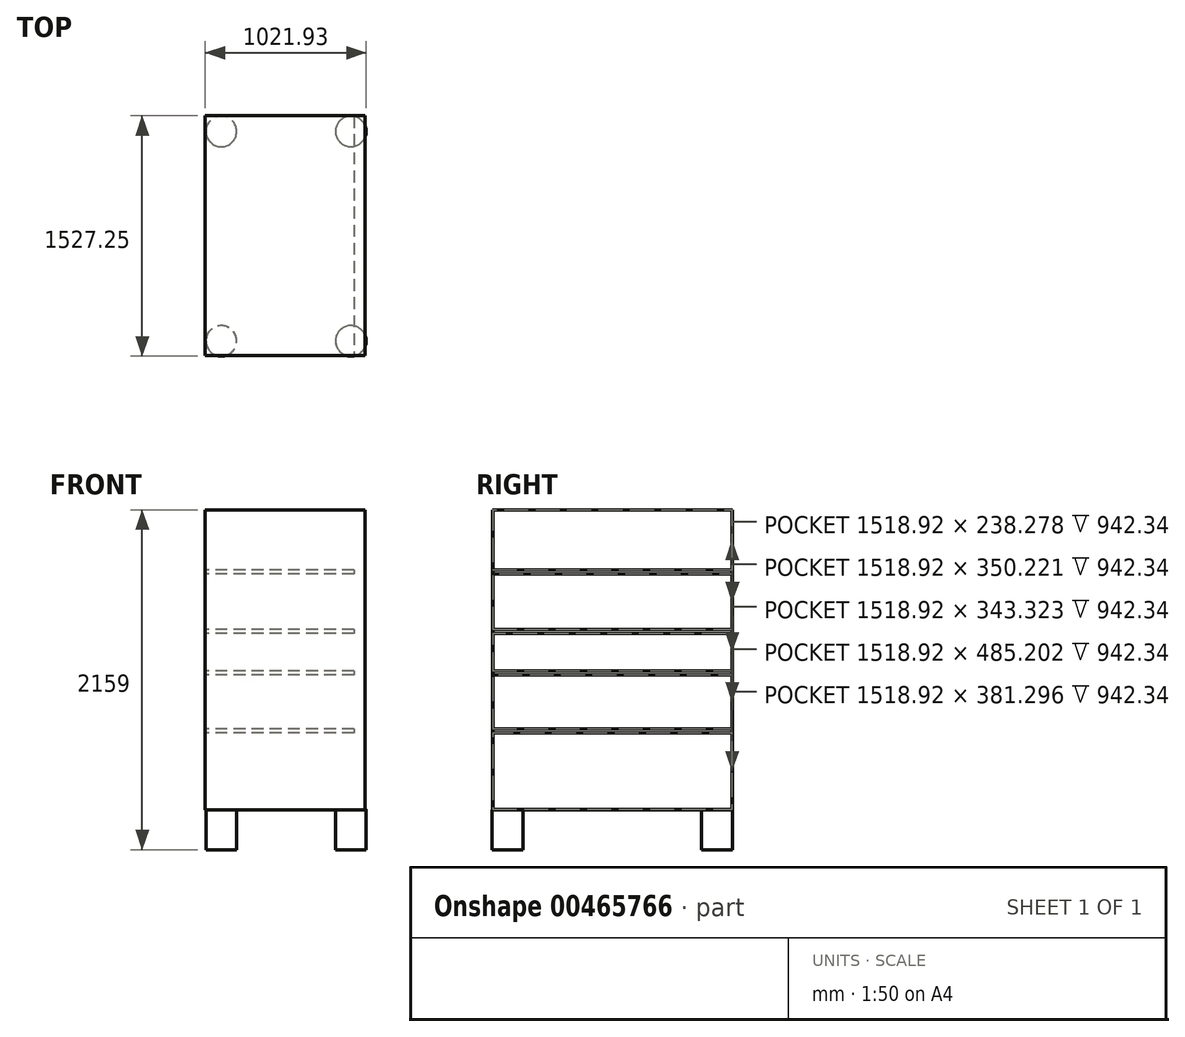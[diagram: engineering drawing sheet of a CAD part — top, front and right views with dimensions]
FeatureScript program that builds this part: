
annotation { "Feature Type Name" : "Feature", "Feature Type Description" : "" }
export const myFeature = defineFeature(function(context is Context, id is Id, definition is map)
    precondition{}
    {
        {
            var Q0;
            Q0=qCreatedBy(makeId("Right.planeOp"),FACE);
            var sketch = newSketch(context, id + "F0", { "sketchPlane" : qUnion([Q0])});
            skLineSegment(sketch, "E0.bottom", {"start": v(-808.5, 938.65) * mm, "end": v(715.5, 938.65) * mm});
            skLineSegment(sketch, "E0.top", {"start": v(-808.5, -966.35) * mm, "end": v(715.5, -966.35) * mm});
            skLineSegment(sketch, "E0.left", {"start": v(-808.5, 938.65) * mm, "end": v(-808.5, -966.35) * mm});
            skLineSegment(sketch, "E0.right", {"start": v(715.5, 938.65) * mm, "end": v(715.5, -966.35) * mm});
            skSolve(sketch);
        }
        {
            var Q0;
            Q0=makeQuery(id+"F0.imprint","IMPRINT",FACE,{"disambiguationData":[TD([[makeQuery(id+"F0.imprint","IMPRINT",EDGE,{"derivedFrom":sQuery(id+"F0.wireOp",EDGE,"E0.bottom")}),-1.0]])]});
            extrude(context, id + "F1", {"entities" : qUnion([Q0]), "depth" : 1016 * mm});
        }
        {
            var Q0;
            Q0=makeQuery(id+"F1.opExtrude","CAP_FACE",FACE,{"disambiguationData":[OSD([sQuery(id+"F0.wireOp",EDGE,"E0.bottom"),sQuery(id+"F0.wireOp",EDGE,"E0.top"),sQuery(id+"F0.wireOp",EDGE,"E0.left"),sQuery(id+"F0.wireOp",EDGE,"E0.right")])],"isStart":false});
            shell(context, id + "F2", {"entities" : qUnion([Q0]), "thickness" : 2.54 * mm});
        }
        {
            var Q0;
            Q0=makeQuery(id+"F2.opShell","OFFSET_FACE",FACE,{"disambiguationData":[OSD([sQuery(id+"F0.wireOp",EDGE,"E0.bottom"),sQuery(id+"F0.wireOp",EDGE,"E0.top"),sQuery(id+"F0.wireOp",EDGE,"E0.left"),sQuery(id+"F0.wireOp",EDGE,"E0.right")])]});
            var sketch = newSketch(context, id + "F3", { "sketchPlane" : qUnion([Q0])});
            skLineSegment(sketch, "E1.bottom", {"start": v(712.96, -453.21) * mm, "end": v(-805.96, -453.21) * mm});
            skLineSegment(sketch, "E1.top", {"start": v(712.96, -478.61) * mm, "end": v(-805.96, -478.61) * mm});
            skLineSegment(sketch, "E1.left", {"start": v(712.96, -453.21) * mm, "end": v(712.96, -478.61) * mm});
            skLineSegment(sketch, "E1.right", {"start": v(-805.96, -453.21) * mm, "end": v(-805.96, -478.61) * mm});
            skLineSegment(sketch, "E2.bottom", {"start": v(712.96, 529.41) * mm, "end": v(-805.96, 529.41) * mm});
            skLineSegment(sketch, "E2.top", {"start": v(712.96, 554.81) * mm, "end": v(-805.96, 554.81) * mm});
            skLineSegment(sketch, "E2.left", {"start": v(712.96, 529.41) * mm, "end": v(712.96, 554.81) * mm});
            skLineSegment(sketch, "E2.right", {"start": v(-805.96, 529.41) * mm, "end": v(-805.96, 554.81) * mm});
            skLineSegment(sketch, "E3.bottom", {"start": v(-805.96, 179.2) * mm, "end": v(712.96, 179.2) * mm});
            skLineSegment(sketch, "E3.top", {"start": v(-805.96, 153.8) * mm, "end": v(712.96, 153.8) * mm});
            skLineSegment(sketch, "E3.left", {"start": v(-805.96, 179.2) * mm, "end": v(-805.96, 153.8) * mm});
            skLineSegment(sketch, "E3.right", {"start": v(712.96, 179.2) * mm, "end": v(712.96, 153.8) * mm});
            skLineSegment(sketch, "E4.bottom", {"start": v(-805.96, -84.49) * mm, "end": v(712.96, -84.49) * mm});
            skLineSegment(sketch, "E4.top", {"start": v(-805.96, -109.89) * mm, "end": v(712.96, -109.89) * mm});
            skLineSegment(sketch, "E4.left", {"start": v(-805.96, -84.49) * mm, "end": v(-805.96, -109.89) * mm});
            skLineSegment(sketch, "E4.right", {"start": v(712.96, -84.49) * mm, "end": v(712.96, -109.89) * mm});
            skSolve(sketch);
        }
        {
            var Q0;
            Q0 = qSketchRegion(id + "F3", true);
            extrude(context, id + "F4", {"entities" : qUnion([Q0]), "operationType" : NewBodyOperationType.ADD, "depth" : 942.34 * mm});
        }
        {
            var Q0;
            Q0=makeQuery(id+"F1.opExtrude","SWEPT_FACE",FACE,{"disambiguationData":[OSD([sQuery(id+"F0.wireOp",EDGE,"E0.top")])]});
            var sketch = newSketch(context, id + "F5", { "sketchPlane" : qUnion([Q0])});
            skCircle(sketch, "E5", {"center": v(924.56, 714.37) * mm, "radius": 97.37 * mm});
            skCircle(sketch, "E6.0.1.0", {"center": v(924.56, -616.59) * mm, "radius": 97.37 * mm});
            skCircle(sketch, "E6.1.0.0", {"center": v(101.6, 714.37) * mm, "radius": 97.37 * mm});
            skCircle(sketch, "E6.1.1.0", {"center": v(101.6, -616.59) * mm, "radius": 97.37 * mm});
            skLineSegment(sketch, "E6.direction1", {"start": v(924.56, 714.37) * mm, "end": v(101.6, 714.37) * mm, "construction": true});
            skLineSegment(sketch, "E6.direction2", {"start": v(924.56, 714.37) * mm, "end": v(924.56, -616.59) * mm, "construction": true});
            skSolve(sketch);
        }
        {
            var Q0;
            Q0 = qSketchRegion(id + "F5", true);
            extrude(context, id + "F6", {"entities" : qUnion([Q0]), "operationType" : NewBodyOperationType.ADD, "depth" : 254 * mm});
        }
    });
